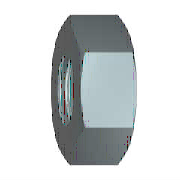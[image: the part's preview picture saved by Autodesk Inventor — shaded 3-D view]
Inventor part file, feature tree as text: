
AUTODESK INVENTOR PART (.ipt)
format: ipt  version: 2022 (Build 260153000, 153)  size: 173,056 bytes
history: native  units: mm (DEFAULTED — no unit token found)
features: sketch x3, chamfer x1, hole x1, other x1, plane x1
ambient origin geometry x7: Origin, YZ Plane, XZ Plane, X Axis, Y Axis, Z Axis, Center Point
bodies: Solid1 (feature_tree), Body (feature_tree)
feature tree (7):
  chamfer  "Chamfer1"  Angle=30.0deg  [1 undecoded]
  hole  "Thread"  [1 undecoded]
  other  "Work Axis1"
  plane  "Work Plane1"
  sketch  "Sketch1"  dims[d0=9.237604mm]
  sketch  "Sketch2"  dims[d1=4.7mm]
  sketch  "Sketch3"  dims[d2=0.0mm d3=30.0deg d4=30.0deg d5=8.0mm d6=8.0mm d7=90.0deg d25=4.134mm d26=6.0mm d27=4.0mm d28=2.0mm d29=14.3117mm d30=8.0mm d31=20.594885mm d8=0.433013mm d9=30.0deg d10=0.433013mm d11=30.0deg d13=0.0mm d14=0.0mm d39=0.0mm d40=0.433013mm d41=0.433013mm d42=0.0mm]
note: 2 required parameter values undecoded (feature->parameter linkage not recoverable at this tier; creation-order binding heuristic only, values carry confidence <= 0.55)
